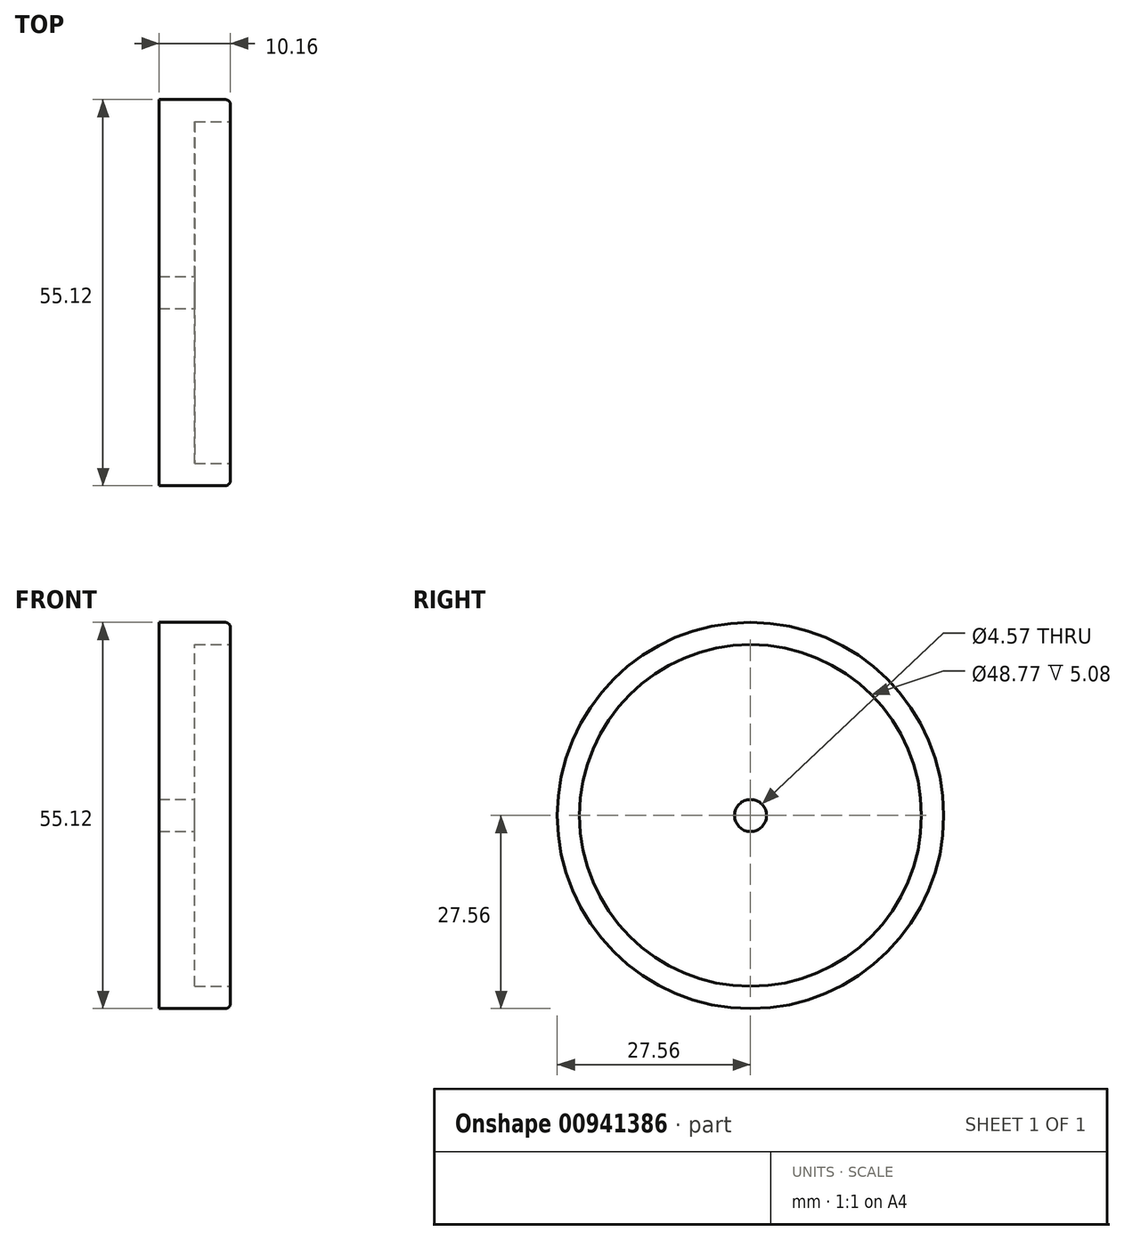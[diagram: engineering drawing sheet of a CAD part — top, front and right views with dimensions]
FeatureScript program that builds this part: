
annotation { "Feature Type Name" : "Feature", "Feature Type Description" : "" }
export const myFeature = defineFeature(function(context is Context, id is Id, definition is map)
    precondition{}
    {
        {
            var Q0;
            Q0=qCreatedBy(makeId("Front.planeOp"),FACE);
            var sketch = newSketch(context, id + "F0", { "sketchPlane" : qUnion([Q0])});
            skLineSegment(sketch, "E0", {"start": v(0, 2.29) * mm, "end": v(0, 27.56) * mm});
            skLineSegment(sketch, "E1", {"start": v(0, 27.56) * mm, "end": v(9.4, 27.56) * mm});
            skLineSegment(sketch, "E2", {"start": v(10.16, 26.8) * mm, "end": v(10.16, 24.38) * mm});
            skLineSegment(sketch, "E3", {"start": v(10.16, 24.38) * mm, "end": v(5.08, 24.38) * mm});
            skLineSegment(sketch, "E4", {"start": v(5.08, 24.38) * mm, "end": v(5.08, 2.29) * mm});
            skLineSegment(sketch, "E5", {"start": v(5.08, 0) * mm, "end": v(0, 0) * mm});
            skPoint(sketch, "E6.visualSharp", {"position": v(10.16, 27.56) * mm});
            skArc(sketch, "E6.filletArc", {"start": v(10.16, 26.8) * mm, "mid": v(9.94, 27.34) * mm, "end": v(9.4, 27.56) * mm});
            skLineSegment(sketch, "E7.0", {"start": v(5.08, 2.29) * mm, "end": v(0, 2.29) * mm});
            skSolve(sketch);
        }
        {
            var Q0;
            Q0=makeQuery(id+"F0.imprint","IMPRINT",FACE,{"disambiguationData":[TD([[makeQuery(id+"F0.imprint","IMPRINT",EDGE,{"derivedFrom":sQuery(id+"F0.wireOp",EDGE,"E0")}),-1.0]])]});
            var Q1;
            Q1=sQuery(id+"F0.wireOp",EDGE,"E5");
            revolve(context, id + "F1", {"surfaceOperationType" : NewSurfaceOperationType.NEW, "entities" : qUnion([Q0]), "axis" : qUnion([Q1]), "revolveType" : RevolveType.FULL});
        }
    });
